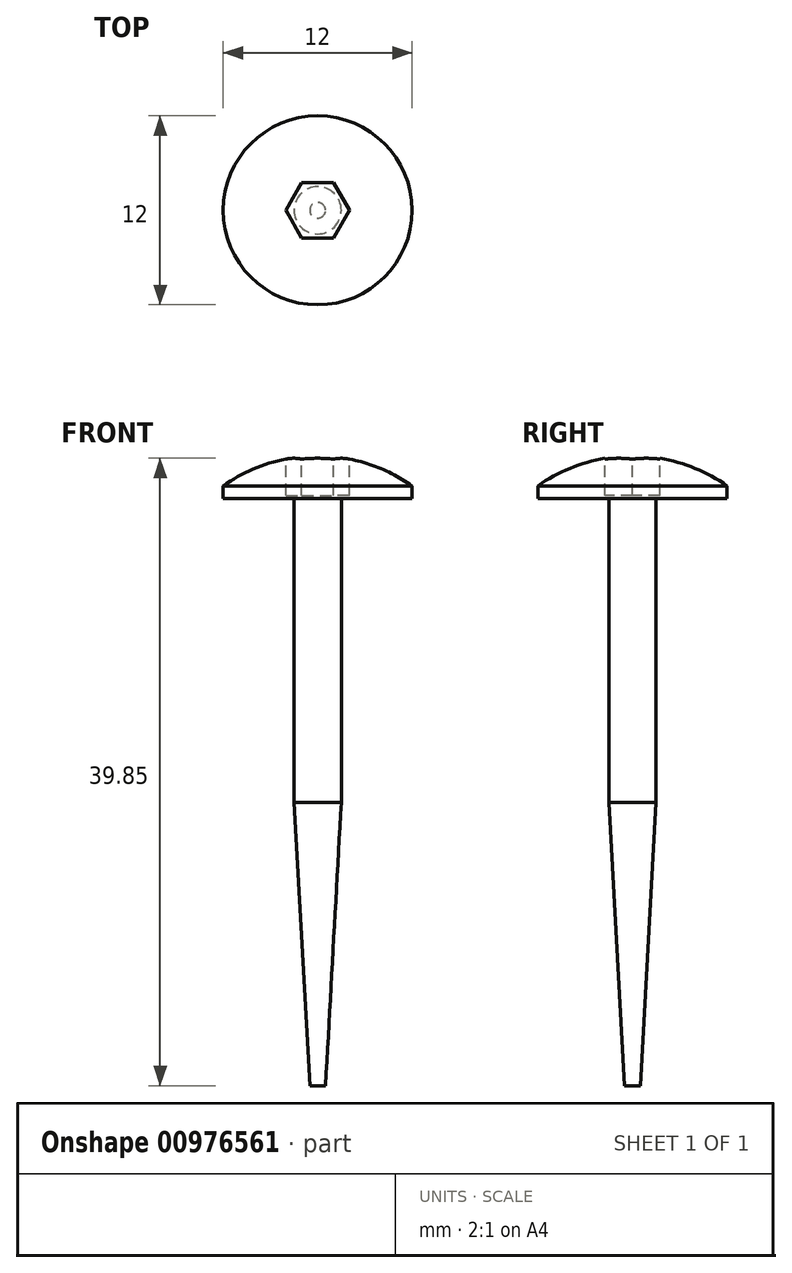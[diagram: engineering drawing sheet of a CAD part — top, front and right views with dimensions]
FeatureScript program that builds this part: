
annotation { "Feature Type Name" : "Feature", "Feature Type Description" : "" }
export const myFeature = defineFeature(function(context is Context, id is Id, definition is map)
    precondition{}
    {
        {
            var Q0;
            Q0=qCreatedBy(makeId("Front.planeOp"),FACE);
            var sketch = newSketch(context, id + "F0", { "sketchPlane" : qUnion([Q0])});
            skLineSegment(sketch, "E0", {"start": v(0, 0) * mm, "end": v(0, -40) * mm});
            skLineSegment(sketch, "E1", {"start": v(0, -40) * mm, "end": v(-1.5, -40) * mm});
            skLineSegment(sketch, "E2", {"start": v(-1.5, -40) * mm, "end": v(-1.5, -2.7) * mm});
            skLineSegment(sketch, "E3", {"start": v(-1.5, -2.7) * mm, "end": v(-6, -2.7) * mm});
            skLineSegment(sketch, "E4", {"start": v(-6, -2.7) * mm, "end": v(-6, -1.9) * mm});
            skArc(sketch, "E5", {"start": v(0, 0) * mm, "mid": v(-3.15, -0.49) * mm, "end": v(-6, -1.9) * mm});
            skLineSegment(sketch, "E6", {"start": v(0, 0) * mm, "end": v(-6, 0) * mm, "construction": true});
            skLineSegment(sketch, "E7", {"start": v(-6, 0) * mm, "end": v(-6, -1.9) * mm, "construction": true});
            skSolve(sketch);
        }
        {
            var Q0;
            Q0=makeQuery(id+"F0.imprint","IMPRINT",FACE,{"disambiguationData":[TD([[makeQuery(id+"F0.imprint","IMPRINT",EDGE,{"derivedFrom":sQuery(id+"F0.wireOp",EDGE,"E0")}),-1.0]])]});
            var Q1;
            Q1=sQuery(id+"F0.wireOp",EDGE,"E0");
            revolve(context, id + "F1", {"surfaceOperationType" : NewSurfaceOperationType.NEW, "entities" : qUnion([Q0]), "axis" : qUnion([Q1]), "revolveType" : RevolveType.FULL});
        }
        {
            var Q0;
            Q0=makeQuery(id+"F1.opRevolve","SWEPT_EDGE",EDGE,{"disambiguationData":[OSD([sQuery(id+"F0.wireOp",EDGE,"E1"),sQuery(id+"F0.wireOp",EDGE,"E2")])]});
            chamfer(context, id + "F2", {"entities" : qUnion([Q0]), "chamferType" : ChamferType.TWO_OFFSETS, "width1" : 18 * mm, "oppositeDirection" : false, "width2" : 1 * mm, "tangentPropagation" : true});
        }
        {
            var Q0;
            Q0=qCreatedBy(makeId("Top.planeOp"),FACE);
            var sketch = newSketch(context, id + "F3", { "sketchPlane" : qUnion([Q0])});
            skCircle(sketch, "E8.cCircle", {"center": v(0, 0) * mm, "radius": 1.75 * mm, "construction": true});
            skLineSegment(sketch, "E8.0", {"start": v(2.02, 0) * mm, "end": v(1.01, -1.75) * mm});
            skLineSegment(sketch, "E8.1", {"start": v(1.01, -1.75) * mm, "end": v(-1.01, -1.75) * mm});
            skLineSegment(sketch, "E8.2", {"start": v(-1.01, -1.75) * mm, "end": v(-2.02, 0) * mm});
            skLineSegment(sketch, "E8.3", {"start": v(-2.02, 0) * mm, "end": v(-1.01, 1.75) * mm});
            skLineSegment(sketch, "E8.4", {"start": v(-1.01, 1.75) * mm, "end": v(1.01, 1.75) * mm});
            skLineSegment(sketch, "E8.5", {"start": v(1.01, 1.75) * mm, "end": v(2.02, 0) * mm});
            skPoint(sketch, "E8.0.midPoint", {"position": v(1.52, -0.88) * mm});
            skSolve(sketch);
        }
        {
            var Q0;
            Q0=makeQuery(id+"F3.imprint","IMPRINT",FACE,{"disambiguationData":[TD([[makeQuery(id+"F3.imprint","IMPRINT",EDGE,{"derivedFrom":sQuery(id+"F3.wireOp",EDGE,"E8.0")}),-1.0]])]});
            extrude(context, id + "F4", {"entities" : qUnion([Q0]), "operationType" : NewBodyOperationType.REMOVE, "oppositeDirection" : true, "depth" : 2.5 * mm, "offsetDistance" : 25 * mm});
        }
    });
